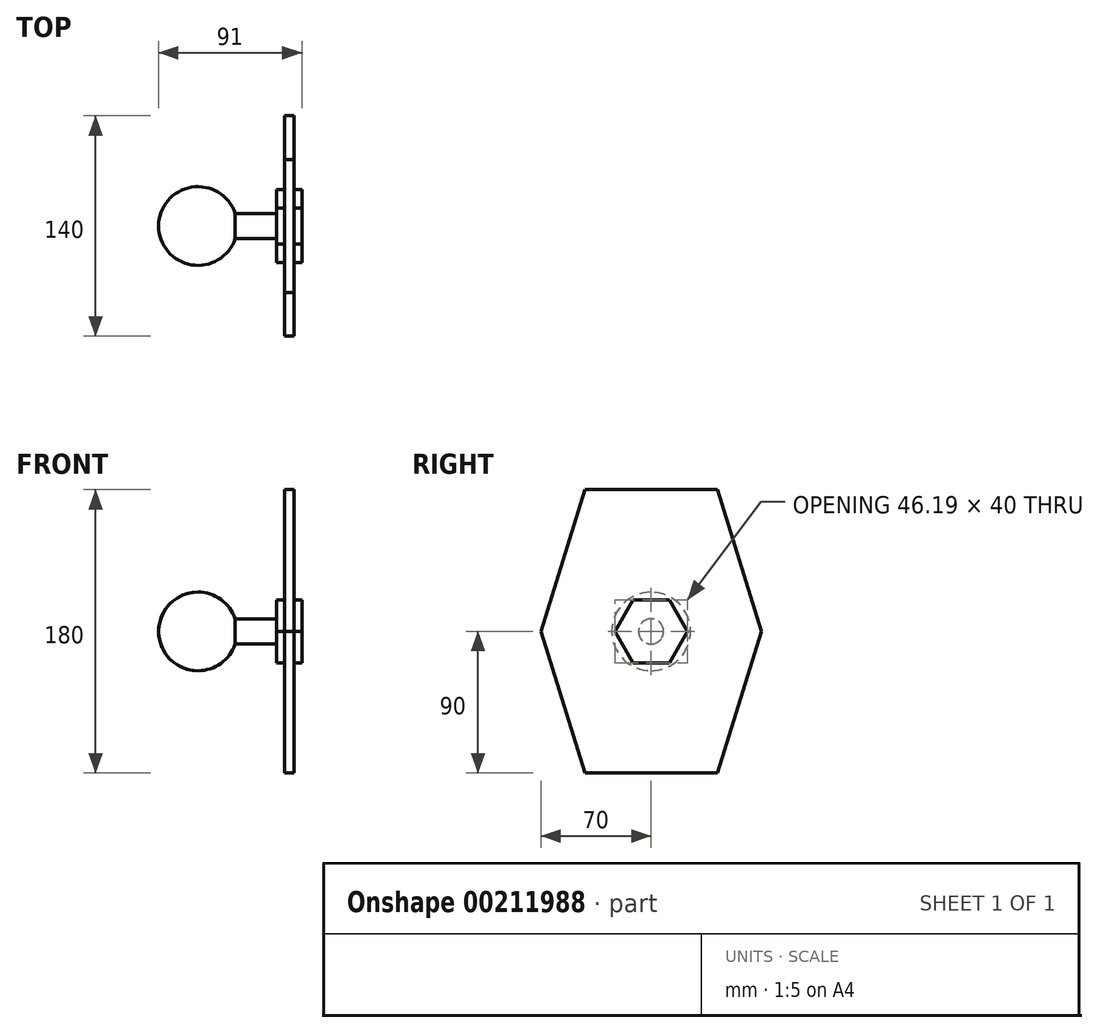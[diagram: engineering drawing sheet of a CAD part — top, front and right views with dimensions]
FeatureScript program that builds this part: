
annotation { "Feature Type Name" : "Feature", "Feature Type Description" : "" }
export const myFeature = defineFeature(function(context is Context, id is Id, definition is map)
    precondition{}
    {
        {
            var Q0;
            Q0=qCreatedBy(makeId("Front.planeOp"),FACE);
            var sketch = newSketch(context, id + "F0", { "sketchPlane" : qUnion([Q0])});
            skArc(sketch, "E0", {"start": v(0, 25) * mm, "mid": v(-25, 0) * mm, "end": v(0, -25) * mm});
            skLineSegment(sketch, "E1", {"start": v(0, 25) * mm, "end": v(0, -25) * mm});
            skSolve(sketch);
        }
        {
            var Q0;
            Q0 = qSketchRegion(id + "F0", true);
            var Q1;
            Q1=sQuery(id+"F0.wireOp",EDGE,"E1");
            revolve(context, id + "F1", {"entities" : qUnion([Q0]), "axis" : qUnion([Q1]), "revolveType" : RevolveType.FULL});
        }
        {
            var Q0;
            Q0=qCreatedBy(makeId("Right.planeOp"),FACE);
            var sketch = newSketch(context, id + "F2", { "sketchPlane" : qUnion([Q0])});
            skCircle(sketch, "E2", {"center": v(0, 0) * mm, "radius": 8 * mm});
            skSolve(sketch);
        }
        {
            var Q0;
            Q0 = qSketchRegion(id + "F2", true);
            extrude(context, id + "F3", {"entities" : qUnion([Q0]), "operationType" : NewBodyOperationType.ADD, "depth" : 55 * mm});
        }
        {
            var Q0;
            Q0=makeQuery(id+"F3.opExtrude","CAP_FACE",FACE,{"disambiguationData":[OSD([sQuery(id+"F2.wireOp",EDGE,"E2")])],"isStart":false});
            var sketch = newSketch(context, id + "F4", { "sketchPlane" : qUnion([Q0])});
            skLineSegment(sketch, "E3", {"start": v(-70, 0) * mm, "end": v(-42.14, 90) * mm});
            skLineSegment(sketch, "E4", {"start": v(0, 0) * mm, "end": v(80.65, 0) * mm, "construction": true});
            skLineSegment(sketch, "E5", {"start": v(0, 0) * mm, "end": v(0, 65.76) * mm, "construction": true});
            skLineSegment(sketch, "E6.MirrorCS", {"start": v(70, 0) * mm, "end": v(42.14, 90) * mm});
            skLineSegment(sketch, "E7", {"start": v(-42.14, 90) * mm, "end": v(42.14, 90) * mm});
            skLineSegment(sketch, "E8.MirrorCS", {"start": v(-70, 0) * mm, "end": v(-42.14, -90) * mm});
            skLineSegment(sketch, "E9.MirrorCS", {"start": v(-42.14, -90) * mm, "end": v(42.14, -90) * mm});
            skLineSegment(sketch, "E10.MirrorCS", {"start": v(70, 0) * mm, "end": v(42.14, -90) * mm});
            skSolve(sketch);
        }
        {
            var Q0;
            Q0 = qSketchRegion(id + "F4", true);
            extrude(context, id + "F5", {"entities" : qUnion([Q0]), "operationType" : NewBodyOperationType.ADD, "depth" : 6 * mm});
        }
        {
            var Q0;
            Q0=makeQuery(id+"F5.opExtrude","CAP_FACE",FACE,{"disambiguationData":[OSD([sQuery(id+"F4.wireOp",EDGE,"E3"),sQuery(id+"F4.wireOp",EDGE,"E6.MirrorCS"),sQuery(id+"F4.wireOp",EDGE,"E7"),sQuery(id+"F4.wireOp",EDGE,"E8.MirrorCS"),sQuery(id+"F4.wireOp",EDGE,"E9.MirrorCS"),sQuery(id+"F4.wireOp",EDGE,"E10.MirrorCS")])],"isStart":false});
            var sketch = newSketch(context, id + "F6", { "sketchPlane" : qUnion([Q0])});
            skCircle(sketch, "E11.cCircle", {"center": v(0, 0) * mm, "radius": 20 * mm, "construction": true});
            skLineSegment(sketch, "E11.0", {"start": v(11.55, -20) * mm, "end": v(-11.55, -20) * mm});
            skLineSegment(sketch, "E11.1", {"start": v(-11.55, -20) * mm, "end": v(-23.1, 0) * mm});
            skLineSegment(sketch, "E11.2", {"start": v(-23.1, 0) * mm, "end": v(-11.55, 20) * mm});
            skLineSegment(sketch, "E11.3", {"start": v(-11.55, 20) * mm, "end": v(11.55, 20) * mm});
            skLineSegment(sketch, "E11.4", {"start": v(11.55, 20) * mm, "end": v(23.1, 0) * mm});
            skLineSegment(sketch, "E11.5", {"start": v(23.1, 0) * mm, "end": v(11.55, -20) * mm});
            skPoint(sketch, "E11.0.midPoint", {"position": v(0, -20) * mm});
            skSolve(sketch);
        }
        {
            var Q0;
            Q0 = qSketchRegion(id + "F6", true);
            extrude(context, id + "F7", {"entities" : qUnion([Q0]), "operationType" : NewBodyOperationType.ADD, "depth" : 5 * mm, "hasSecondDirection" : true, "secondDirectionOppositeDirection" : true, "secondDirectionDepth" : 11 * mm});
        }
    });
